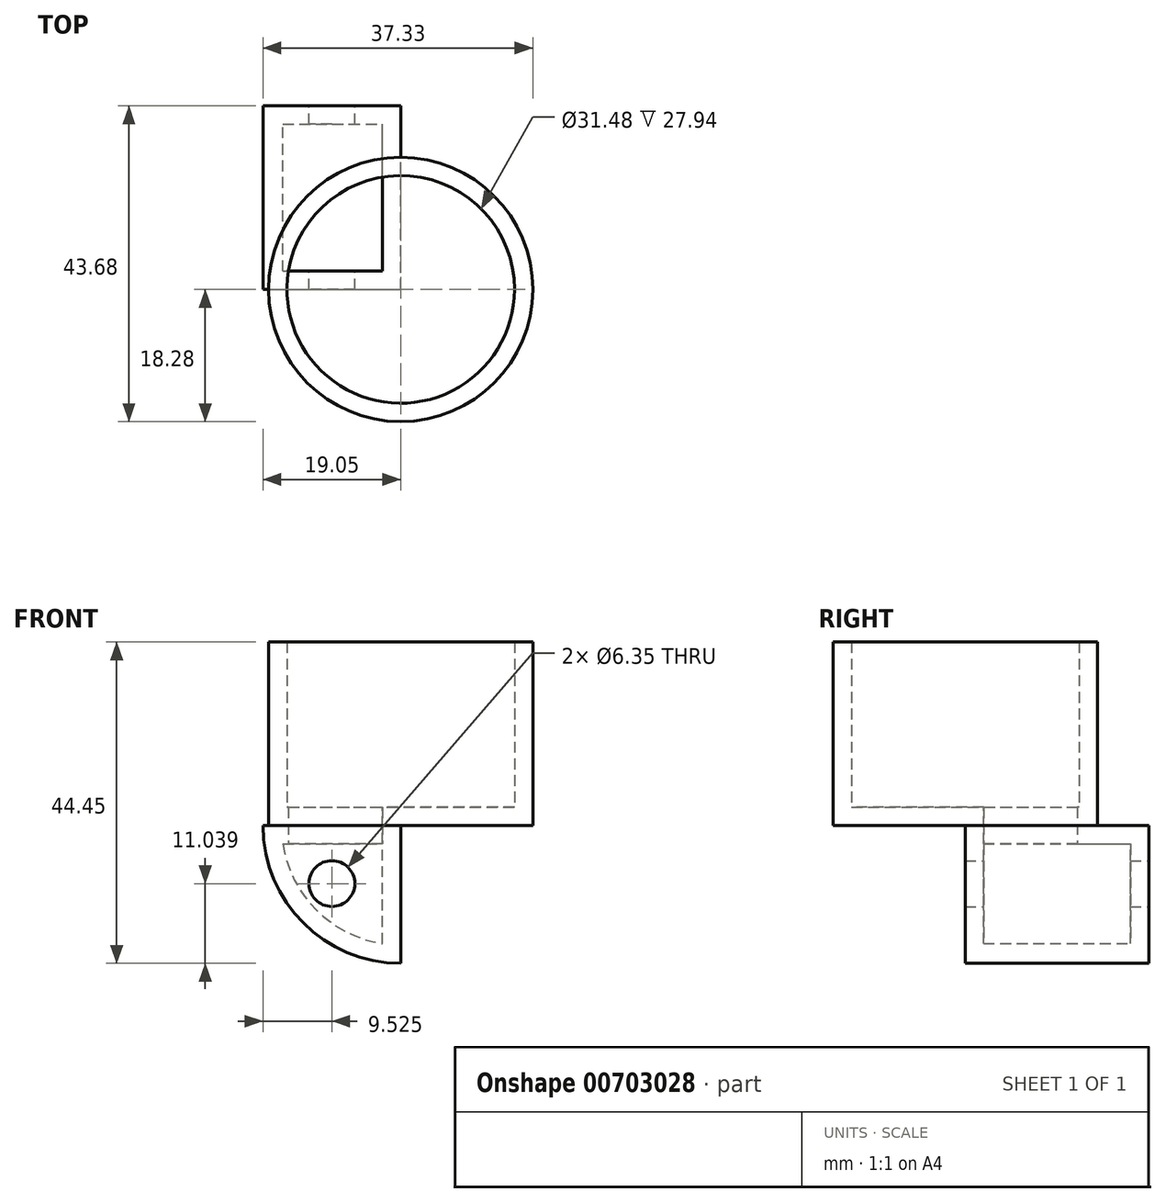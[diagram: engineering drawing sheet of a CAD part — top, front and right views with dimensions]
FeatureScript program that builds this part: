
annotation { "Feature Type Name" : "Feature", "Feature Type Description" : "" }
export const myFeature = defineFeature(function(context is Context, id is Id, definition is map)
    precondition{}
    {
        {
            var Q0;
            Q0=qCreatedBy(makeId("Front.planeOp"),FACE);
            var sketch = newSketch(context, id + "F0", { "sketchPlane" : qUnion([Q0])});
            skLineSegment(sketch, "E0.bottom", {"start": v(0, 0) * mm, "end": v(50.8, 0) * mm});
            skLineSegment(sketch, "E0.top", {"start": v(0, 38.1) * mm, "end": v(50.8, 38.1) * mm});
            skLineSegment(sketch, "E0.left", {"start": v(0, 0) * mm, "end": v(0, 38.1) * mm});
            skLineSegment(sketch, "E0.right", {"start": v(50.8, 0) * mm, "end": v(50.8, 38.1) * mm});
            skCircle(sketch, "E1", {"center": v(50.8, 38.1) * mm, "radius": 19.05 * mm});
            skSolve(sketch);
        }
        {
            var Q0;
            {var subQ0=sQuery(id+"F0.wireOp",EDGE,"E0.right");var subQ1=sQuery(id+"F0.wireOp",EDGE,"E0.top");var subQ2=makeQuery(id+"F0.imprint","INTERSECT",VERTEX,{"derivedFrom":[subQ1,subQ0]});Q0=makeQuery(id+"F0.imprint","IMPRINT",FACE,{"disambiguationData":[TD([[makeQuery(id+"F0.imprint","IMPRINT",EDGE,{"disambiguationData":[TD([[subQ2,1.0]])],"derivedFrom":subQ1}),-1.0]])]});}
            extrude(context, id + "F1", {"entities" : qUnion([Q0]), "depth" : 25.4 * mm, "offsetDistance" : 25.4 * mm});
        }
        {
            var Q0;
            Q0=makeQuery(id+"F1.opExtrude","SWEPT_FACE",FACE,{"disambiguationData":[OSD([sQuery(id+"F0.wireOp",EDGE,"E0.top")])]});
            var sketch = newSketch(context, id + "F2", { "sketchPlane" : qUnion([Q0])});
            skCircle(sketch, "E2", {"center": v(50.8, -25.4) * mm, "radius": 18.28 * mm});
            skSolve(sketch);
        }
        {
            var Q0;
            Q0 = qSketchRegion(id + "F2", true);
            extrude(context, id + "F3", {"entities" : qUnion([Q0]), "operationType" : NewBodyOperationType.ADD, "depth" : 25.4 * mm, "offsetDistance" : 25.4 * mm});
        }
        {
            var Q0;
            Q0=makeQuery(id+"F3.opExtrude","CAP_FACE",FACE,{"disambiguationData":[OSD([sQuery(id+"F2.wireOp",EDGE,"E2")])],"isStart":false});
            shell(context, id + "F4", {"entities" : qUnion([Q0]), "thickness" : 2.54 * mm});
        }
        {
            var Q0;
            Q0=makeQuery(id+"F1.opExtrude","CAP_FACE",FACE,{"disambiguationData":[OSD([sQuery(id+"F0.wireOp",EDGE,"E0.top"),sQuery(id+"F0.wireOp",EDGE,"E0.right"),sQuery(id+"F0.wireOp",EDGE,"E1")])],"isStart":true});
            var sketch = newSketch(context, id + "F5", { "sketchPlane" : qUnion([Q0])});
            skPoint(sketch, "E3", {"position": v(-41.27, 30.09) * mm});
            skPoint(sketch, "E3.positionSnap0", {"position": v(-41.27, 38.1) * mm});
            skSolve(sketch);
        }
        {
            var Q0;
            Q0=sQuery(id+"F5.wireOp",VERTEX,"E3");
            var Q1;
            Q1=makeQuery(id+"F1.opExtrude","SWEPT_BODY",BODY,{"disambiguationData":[OSD([sQuery(id+"F0.wireOp",EDGE,"E0.top"),sQuery(id+"F0.wireOp",EDGE,"E0.right"),sQuery(id+"F0.wireOp",EDGE,"E1")])]});
            hole(context, id + "F6", {"style" : HoleStyle.SIMPLE, "endStyle" : HoleEndStyle.THROUGH, "holeDiameter" : 6.35 * mm, "majorDiameter" : 6.35 * mm, "isTappedThrough" : true, "tappedDepth" : 12.7 * mm, "tapClearance" : 3, "locations" : qUnion([Q0]), "scope" : qUnion([Q1])});
        }
    });
